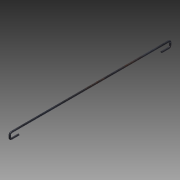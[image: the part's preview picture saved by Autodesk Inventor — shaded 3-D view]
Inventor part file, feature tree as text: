
AUTODESK INVENTOR PART (.ipt)
format: ipt  version: 2011 SP1 (Build 150282100, 282)  size: 80,896 bytes
history: native  units: in
note: dims shown in document units (in); Inventor stores cm internally (conversion verified against a paired STEP export)
features: sketch x2, sweep x1
ambient origin geometry x8: Origin, YZ Plane, XZ Plane, XY Plane, X Axis, Y Axis, Z Axis, Center Point
bodies: Solid1 (feature_tree)
feature tree (3):
  sweep  "Sweep1"
  sketch  "Sketch1"  dims[d0=0.047in d1=0.05in]
  sketch  "Sketch2"  dims[d5=0.0625in d7=4.55in d8=0.25in d9=0.0in]
